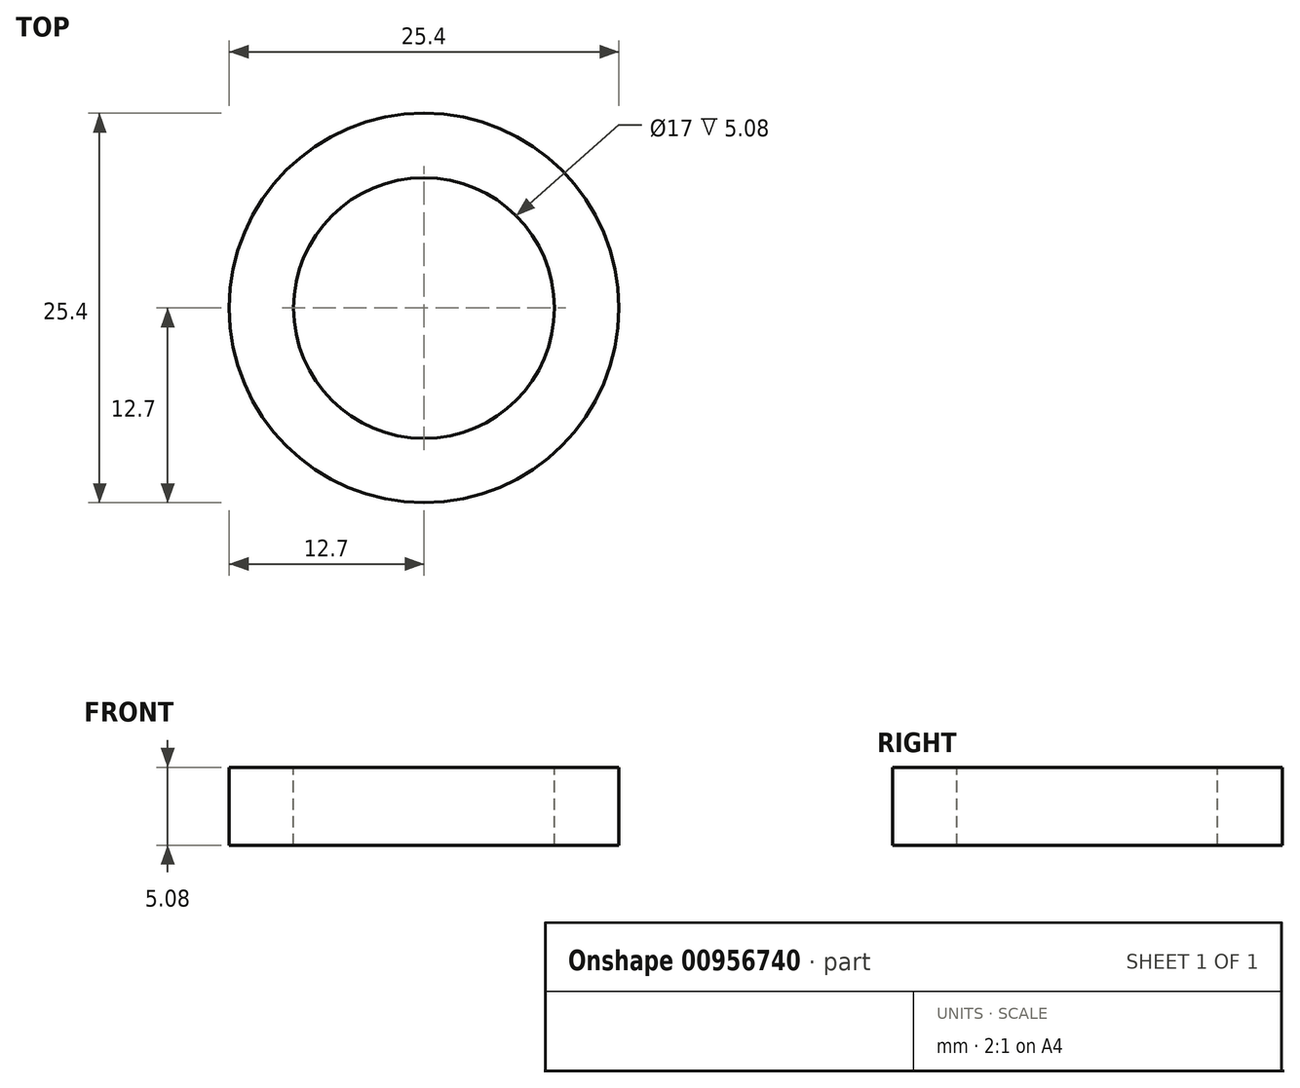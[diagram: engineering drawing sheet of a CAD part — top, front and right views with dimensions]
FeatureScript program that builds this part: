
annotation { "Feature Type Name" : "Feature", "Feature Type Description" : "" }
export const myFeature = defineFeature(function(context is Context, id is Id, definition is map)
    precondition{}
    {
        {
            var Q0;
            Q0=qCreatedBy(makeId("Top.planeOp"),FACE);
            var sketch = newSketch(context, id + "F0", { "sketchPlane" : qUnion([Q0])});
            skCircle(sketch, "E0", {"center": v(0, 0) * mm, "radius": 12.7 * mm});
            skSolve(sketch);
        }
        {
            var Q0;
            Q0 = qSketchRegion(id + "F0", true);
            var Q1;
            Q1=makeQuery(id+"F0.imprint","IMPRINT",FACE,{"disambiguationData":[TD([[makeQuery(id+"F0.imprint","IMPRINT",EDGE,{"derivedFrom":sQuery(id+"F0.wireOp",EDGE,"E0")}),1.0]])]});
            extrude(context, id + "F1", {"entities" : qUnion([Q0, Q1]), "depth" : 5.08 * mm, "offsetDistance" : 25.4 * mm});
        }
        {
            var Q0;
            Q0=makeQuery(id+"F1.opExtrude","CAP_FACE",FACE,{"disambiguationData":[OSD([sQuery(id+"F0.wireOp",EDGE,"E0")])],"isStart":false});
            var sketch = newSketch(context, id + "F2", { "sketchPlane" : qUnion([Q0])});
            skCircle(sketch, "E1", {"center": v(0, 0) * mm, "radius": 8.5 * mm});
            skSolve(sketch);
        }
        {
            var Q0;
            Q0=makeQuery(id+"F2.imprint","IMPRINT",FACE,{"disambiguationData":[TD([[makeQuery(id+"F2.imprint","IMPRINT",EDGE,{"derivedFrom":sQuery(id+"F2.wireOp",EDGE,"E1")}),1.0]])]});
            extrude(context, id + "F3", {"entities" : qUnion([Q0]), "operationType" : NewBodyOperationType.REMOVE, "endBound" : BoundingType.UP_TO_NEXT, "oppositeDirection" : true, "depth" : 25.4 * mm, "offsetDistance" : 25.4 * mm});
        }
    });
